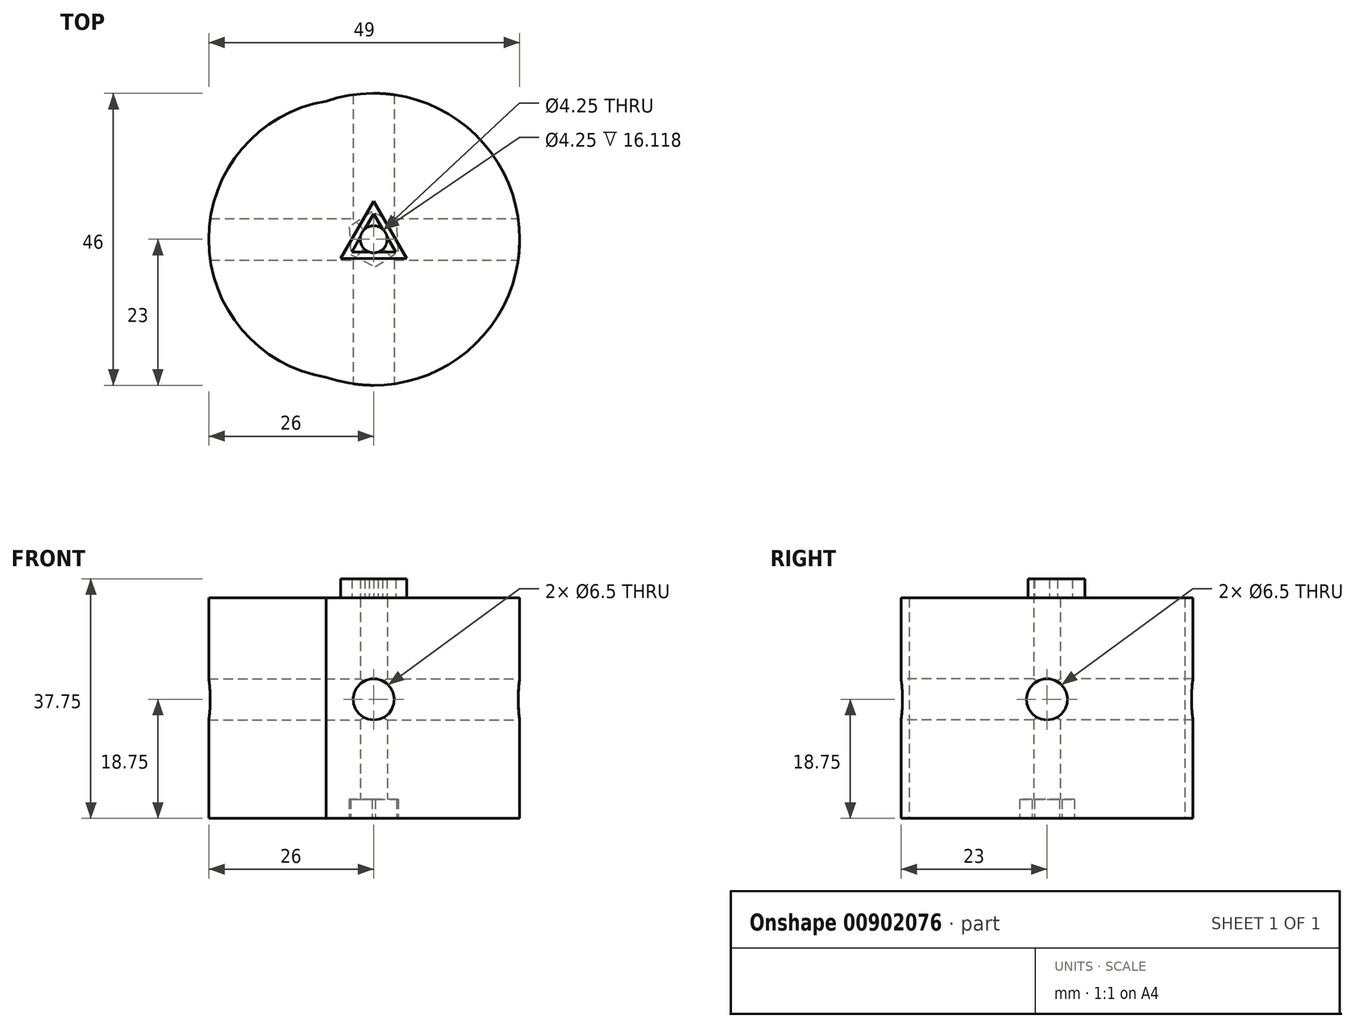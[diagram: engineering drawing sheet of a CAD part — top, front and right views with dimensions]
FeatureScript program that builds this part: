
annotation { "Feature Type Name" : "Feature", "Feature Type Description" : "" }
export const myFeature = defineFeature(function(context is Context, id is Id, definition is map)
    precondition{}
    {
        {
            var Q0;
            Q0=qCreatedBy(makeId("Top.planeOp"),FACE);
            var sketch = newSketch(context, id + "F0", { "sketchPlane" : qUnion([Q0])});
            skCircle(sketch, "E0", {"center": v(0, 0) * mm, "radius": 20 * mm});
            skPoint(sketch, "E1", {"position": v(-11.87, 16.1) * mm});
            skPoint(sketch, "E2.MirrorP", {"position": v(11.87, 16.1) * mm});
            skArc(sketch, "E3", {"start": v(11.87, 16.1) * mm, "mid": v(0, 23) * mm, "end": v(-11.87, 16.1) * mm});
            skArc(sketch, "E4.1.0", {"start": v(-19.88, 2.23) * mm, "mid": v(-19.92, -11.5) * mm, "end": v(-8, -18.33) * mm});
            skArc(sketch, "E4.2.0", {"start": v(8, -18.33) * mm, "mid": v(19.92, -11.5) * mm, "end": v(19.88, 2.23) * mm});
            skSolve(sketch);
        }
        {
            var Q0;
            Q0=makeQuery(id+"F0.imprint","IMPRINT",FACE,{"disambiguationData":[TD([[makeQuery(id+"F0.imprint","IMPRINT",EDGE,{"derivedFrom":sQuery(id+"F0.wireOp",EDGE,"iPbp3OPt-Og0e-h1Yw-MaBf-0AZW6OAXDtnJ")}),-1.0]])]});
            var Q1;
            {var subQ0=sQuery(id+"F0.wireOp",EDGE,"E3");Q1=makeQuery(id+"F0.imprint","IMPRINT",FACE,{"disambiguationData":[TD([[makeQuery(id+"F0.imprint","IMPRINT",EDGE,{"derivedFrom":subQ0}),1.0]])]});}
            var Q2;
            {var subQ0=sQuery(id+"F0.wireOp",EDGE,"E4.1.0");Q2=makeQuery(id+"F0.imprint","IMPRINT",FACE,{"disambiguationData":[TD([[makeQuery(id+"F0.imprint","IMPRINT",EDGE,{"derivedFrom":subQ0}),1.0]])]});}
            var Q3;
            {var subQ0=sQuery(id+"F0.wireOp",EDGE,"E4.2.0");Q3=makeQuery(id+"F0.imprint","IMPRINT",FACE,{"disambiguationData":[TD([[makeQuery(id+"F0.imprint","IMPRINT",EDGE,{"derivedFrom":subQ0}),1.0]])]});}
            var Q4;
            Q4=makeQuery(id+"F0.imprint","IMPRINT",FACE,{"disambiguationData":[TD([[makeQuery(id+"F0.imprint","IMPRINT",EDGE,{"derivedFrom":sQuery(id+"F0.wireOp",EDGE,"6CoMubdr-rplY-xLew-Zasb-LncCztSGb2TN")}),-1.0]])]});
            var Q5;
            {var subQ1=sQuery(id+"F0.wireOp",EDGE,"E0");var subQ4=sQuery(id+"F0.wireOp",EDGE,"E3");var subQ6=makeQuery(id+"F0.imprint","INTERSECT",VERTEX,{"disambiguationData":[OD(0.0)],"derivedFrom":[subQ1,subQ4]});Q5=makeQuery(id+"F0.imprint","IMPRINT",FACE,{"disambiguationData":[TD([[makeQuery(id+"F0.imprint","IMPRINT",EDGE,{"disambiguationData":[TD([[subQ6,1.0]])],"derivedFrom":subQ1}),1.0]])]});}
            extrude(context, id + "F1", {"entities" : qUnion([Q0, Q1, Q2, Q3, Q4, Q5]), "depth" : 12 * mm, "offsetDistance" : 25 * mm});
        }
        {
            var Q0;
            Q0=qCreatedBy(makeId("Front.planeOp"),FACE);
            cPlane(context, id + "F2", {"entities" : qUnion([Q0]), "cplaneType" : CPlaneType.OFFSET, "offset" : 0 * mm, "width" : 150 * mm, "height" : 150 * mm});
        }
        {
            var Q0;
            Q0=qCreatedBy(id+"F2.planeOp",FACE);
            var sketch = newSketch(context, id + "F3", { "sketchPlane" : qUnion([Q0])});
            skPoint(sketch, "E5", {"position": v(0, 6) * mm});
            skCircle(sketch, "E6", {"center": v(0, 6) * mm, "radius": 3.25 * mm});
            skSolve(sketch);
        }
        {
            var Q0;
            Q0=makeQuery(id+"F3.imprint","IMPRINT",FACE,{"disambiguationData":[TD([[makeQuery(id+"F3.imprint","IMPRINT",EDGE,{"derivedFrom":sQuery(id+"F3.wireOp",EDGE,"E6")}),1.0]])]});
            extrude(context, id + "F4", {"entities" : qUnion([Q0]), "operationType" : NewBodyOperationType.REMOVE, "depth" : 25 * mm, "offsetDistance" : 25 * mm, "hasSecondDirection" : true, "secondDirectionOppositeDirection" : true, "secondDirectionDepth" : 25 * mm});
        }
        {
            var Q0;
            Q0=qCreatedBy(makeId("Top.planeOp"),FACE);
            var sketch = newSketch(context, id + "F5", { "sketchPlane" : qUnion([Q0])});
            skCircle(sketch, "E7.cCircle", {"center": v(0, 0) * mm, "radius": 3 * mm, "construction": true});
            skLineSegment(sketch, "E7.0", {"start": v(5.2, -3) * mm, "end": v(-5.2, -3) * mm});
            skLineSegment(sketch, "E7.1", {"start": v(-5.2, -3) * mm, "end": v(0, 6) * mm});
            skLineSegment(sketch, "E7.2", {"start": v(0, 6) * mm, "end": v(5.2, -3) * mm});
            skPoint(sketch, "E7.0.midPoint", {"position": v(0, -3) * mm});
            skCircle(sketch, "E8.cCircle", {"center": v(0, 0) * mm, "radius": 2 * mm, "construction": true});
            skLineSegment(sketch, "E8.0", {"start": v(3.46, -2) * mm, "end": v(-3.46, -2) * mm});
            skLineSegment(sketch, "E8.1", {"start": v(-3.46, -2) * mm, "end": v(0, 4) * mm});
            skLineSegment(sketch, "E8.2", {"start": v(0, 4) * mm, "end": v(3.46, -2) * mm});
            skPoint(sketch, "E8.0.midPoint", {"position": v(0, -2) * mm});
            skSolve(sketch);
        }
        {
            var Q0;
            Q0=makeQuery(id+"F5.imprint","IMPRINT",FACE,{"disambiguationData":[TD([[makeQuery(id+"F5.imprint","IMPRINT",EDGE,{"derivedFrom":sQuery(id+"F5.wireOp",EDGE,"E7.0")}),-1.0]])]});
            extrude(context, id + "F6", {"entities" : qUnion([Q0]), "depth" : 25 * mm, "offsetDistance" : 25 * mm});
        }
        {
            var Q0;
            Q0=makeQuery(id+"F6.opExtrude","SWEPT_FACE",FACE,{"disambiguationData":[OSD([sQuery(id+"F5.wireOp",EDGE,"E7.1")])]});
            var sketch = newSketch(context, id + "F7", { "sketchPlane" : qUnion([Q0])});
            skCircle(sketch, "E9", {"center": v(0, 6) * mm, "radius": 3.25 * mm});
            skSolve(sketch);
        }
        {
            var Q0;
            Q0=makeQuery(id+"F7.imprint","IMPRINT",FACE,{"disambiguationData":[TD([[makeQuery(id+"F7.imprint","IMPRINT",EDGE,{"derivedFrom":sQuery(id+"F7.wireOp",EDGE,"E9")}),1.0]])]});
            extrude(context, id + "F8", {"entities" : qUnion([Q0]), "operationType" : NewBodyOperationType.REMOVE, "depth" : 25 * mm, "offsetDistance" : 25 * mm, "hasSecondDirection" : true, "secondDirectionOppositeDirection" : true, "secondDirectionDepth" : 40 * mm});
        }
        {
            var Q0;
            Q0=makeQuery(id+"F6.opExtrude","SWEPT_FACE",FACE,{"disambiguationData":[OSD([sQuery(id+"F5.wireOp",EDGE,"E7.2")])]});
            var sketch = newSketch(context, id + "F9", { "sketchPlane" : qUnion([Q0])});
            skCircle(sketch, "E10", {"center": v(0, 6) * mm, "radius": 3.25 * mm});
            skSolve(sketch);
        }
        {
            var Q0;
            Q0=makeQuery(id+"F9.imprint","IMPRINT",FACE,{"disambiguationData":[TD([[makeQuery(id+"F9.imprint","IMPRINT",EDGE,{"derivedFrom":sQuery(id+"F9.wireOp",EDGE,"E10")}),1.0]])]});
            extrude(context, id + "F10", {"entities" : qUnion([Q0]), "operationType" : NewBodyOperationType.REMOVE, "depth" : 25 * mm, "offsetDistance" : 25 * mm, "hasSecondDirection" : true, "secondDirectionOppositeDirection" : true, "secondDirectionDepth" : 40 * mm});
        }
        {
            var Q0;
            Q0=qCreatedBy(makeId("Top.planeOp"),FACE);
            var sketch = newSketch(context, id + "F11", { "sketchPlane" : qUnion([Q0])});
            skPoint(sketch, "E11.0", {"position": v(0, 23) * mm});
            skCircle(sketch, "E12", {"center": v(0, 0) * mm, "radius": 23 * mm});
            skArc(sketch, "E13", {"start": v(-7.5, 21.74) * mm, "mid": v(-26, 0) * mm, "end": v(-7.5, -21.74) * mm});
            skArc(sketch, "E14.MirrorCS", {"start": v(7.5, 21.74) * mm, "mid": v(26, 0) * mm, "end": v(7.5, -21.74) * mm});
            skSolve(sketch);
        }
        {
            var Q0;
            Q0=makeQuery(id+"F11.imprint","IMPRINT",FACE,{"disambiguationData":[TD([[makeQuery(id+"F11.imprint","IMPRINT",EDGE,{"derivedFrom":sQuery(id+"F11.wireOp",EDGE,"E12")}),1.0]])]});
            var Q1;
            {var subQ0=sQuery(id+"F11.wireOp",EDGE,"E13");Q1=makeQuery(id+"F11.imprint","IMPRINT",FACE,{"disambiguationData":[TD([[makeQuery(id+"F11.imprint","IMPRINT",EDGE,{"derivedFrom":subQ0}),1.0]])]});}
            var Q2;
            {var subQ0=sQuery(id+"F11.wireOp",EDGE,"E14.MirrorCS");Q2=makeQuery(id+"F11.imprint","IMPRINT",FACE,{"disambiguationData":[TD([[makeQuery(id+"F11.imprint","IMPRINT",EDGE,{"derivedFrom":subQ0}),-1.0]])]});}
            extrude(context, id + "F12", {"entities" : qUnion([Q0, Q1, Q2]), "operationType" : NewBodyOperationType.ADD, "depth" : 22 * mm, "offsetDistance" : 25 * mm, "hasSecondDirection" : true, "secondDirectionOppositeDirection" : true, "secondDirectionDepth" : 12.75 * mm});
        }
        {
            var Q0;
            Q0=makeQuery(id+"F3.imprint","IMPRINT",FACE,{"disambiguationData":[TD([[makeQuery(id+"F3.imprint","IMPRINT",EDGE,{"derivedFrom":sQuery(id+"F3.wireOp",EDGE,"E6")}),1.0]])]});
            extrude(context, id + "F13", {"entities" : qUnion([Q0]), "operationType" : NewBodyOperationType.REMOVE, "oppositeDirection" : true, "depth" : 25 * mm, "offsetDistance" : 25 * mm, "hasSecondDirection" : true, "secondDirectionOppositeDirection" : false, "secondDirectionDepth" : 25 * mm});
        }
        {
            var Q0;
            Q0=qCreatedBy(makeId("Right.planeOp"),FACE);
            var sketch = newSketch(context, id + "F14", { "sketchPlane" : qUnion([Q0])});
            skPoint(sketch, "E15.0", {"position": v(0, 6) * mm});
            skCircle(sketch, "E16", {"center": v(0, 6) * mm, "radius": 3.25 * mm});
            skSolve(sketch);
        }
        {
            var Q0;
            Q0=makeQuery(id+"F14.imprint","IMPRINT",FACE,{"disambiguationData":[TD([[makeQuery(id+"F14.imprint","IMPRINT",EDGE,{"derivedFrom":sQuery(id+"F14.wireOp",EDGE,"E16")}),1.0]])]});
            extrude(context, id + "F15", {"entities" : qUnion([Q0]), "operationType" : NewBodyOperationType.REMOVE, "oppositeDirection" : true, "depth" : 30 * mm, "offsetDistance" : 25 * mm, "hasSecondDirection" : true, "secondDirectionOppositeDirection" : false, "secondDirectionDepth" : 30 * mm});
        }
        {
            var Q0;
            Q0=makeQuery(id+"F12.opExtrude","CAP_FACE",FACE,{"disambiguationData":[OSD([sQuery(id+"F11.wireOp",EDGE,"E12"),sQuery(id+"F11.wireOp",EDGE,"E13"),sQuery(id+"F11.wireOp",EDGE,"E14.MirrorCS")])],"isStart":true});
            var sketch = newSketch(context, id + "F16", { "sketchPlane" : qUnion([Q0])});
            skCircle(sketch, "E17", {"center": v(0, 0) * mm, "radius": 2.12 * mm});
            skCircle(sketch, "E18.cCircle", {"center": v(0, 0) * mm, "radius": 3.75 * mm, "construction": true});
            skLineSegment(sketch, "E18.0", {"start": v(3.62, -2.37) * mm, "end": v(-0.25, -4.32) * mm});
            skLineSegment(sketch, "E18.1", {"start": v(-0.25, -4.32) * mm, "end": v(-3.87, -1.95) * mm});
            skLineSegment(sketch, "E18.2", {"start": v(-3.87, -1.95) * mm, "end": v(-3.62, 2.37) * mm});
            skLineSegment(sketch, "E18.3", {"start": v(-3.62, 2.37) * mm, "end": v(0.25, 4.32) * mm});
            skLineSegment(sketch, "E18.4", {"start": v(0.25, 4.32) * mm, "end": v(3.87, 1.95) * mm});
            skLineSegment(sketch, "E18.5", {"start": v(3.87, 1.95) * mm, "end": v(3.62, -2.37) * mm});
            skPoint(sketch, "E18.0.midPoint", {"position": v(1.69, -3.35) * mm});
            skSolve(sketch);
        }
        {
            var Q0;
            Q0=makeQuery(id+"F16.imprint","IMPRINT",FACE,{"disambiguationData":[TD([[makeQuery(id+"F16.imprint","IMPRINT",EDGE,{"derivedFrom":sQuery(id+"F16.wireOp",EDGE,"E17")}),1.0]])]});
            extrude(context, id + "F17", {"entities" : qUnion([Q0]), "operationType" : NewBodyOperationType.REMOVE, "oppositeDirection" : true, "depth" : 50 * mm, "offsetDistance" : 25 * mm});
        }
        {
            var Q0;
            Q0=makeQuery(id+"F16.imprint","IMPRINT",FACE,{"disambiguationData":[TD([[makeQuery(id+"F16.imprint","IMPRINT",EDGE,{"derivedFrom":sQuery(id+"F16.wireOp",EDGE,"E17")}),-1.0]])]});
            extrude(context, id + "F18", {"entities" : qUnion([Q0]), "operationType" : NewBodyOperationType.REMOVE, "oppositeDirection" : true, "depth" : 3 * mm, "offsetDistance" : 25 * mm});
        }
    });
